AUTODESK INVENTOR PART (.ipt)
format: ipt  version: 2025.1 (Build 291241020, 241B)  size: 216,576 bytes
history: native  units: mm
features: extrude x5, sketch x5, fillet x3, pattern_circular x1
ambient origin geometry x8: Origin, YZ Plane, XZ Plane, XY Plane, X Axis, Y Axis, Z Axis, Center Point
bodies: Solid1 (feature_tree)
feature tree (14):
  extrude  "Extrusion1"  Depth=14.0mm TaperAngle=0.0deg
  extrude  "Extrusion2"  Depth=12.0mm
  pattern_circular  "Circular Pattern1"  Count=4 Angle=360.0deg
  fillet  "Fillet1"  Radius=10.0mm
  extrude  "Extrusion4"  Depth=31.0mm TaperAngle=0.0deg
  extrude  "Extrusion5"  Depth=31.0mm TaperAngle=0.0deg
  extrude  "Extrusion6"  Depth=6.0mm
  fillet  "Fillet2"  Radius=40.0mm
  fillet  "Fillet3"  Radius=3.0mm
  sketch  "Sketch1"  dims[d0=108.0mm d2=14.0mm d3=0.0mm]
  sketch  "Sketch2"  dims[d4=41.5mm d5=12.0mm]
  sketch  "Sketch4"  dims[d6=0.0mm d7=0.0mm d8=40.0mm d9=360.0deg d11=10.0mm]
  sketch  "Sketch5"  dims[d15=70.0mm d16=31.0mm d17=0.0mm]
  sketch  "Sketch6"  dims[d18=30.0mm d19=31.0mm d20=0.0mm d21=6.0mm d22=40.0mm d23=0.0mm d24=3.0mm d25=2.0mm]
